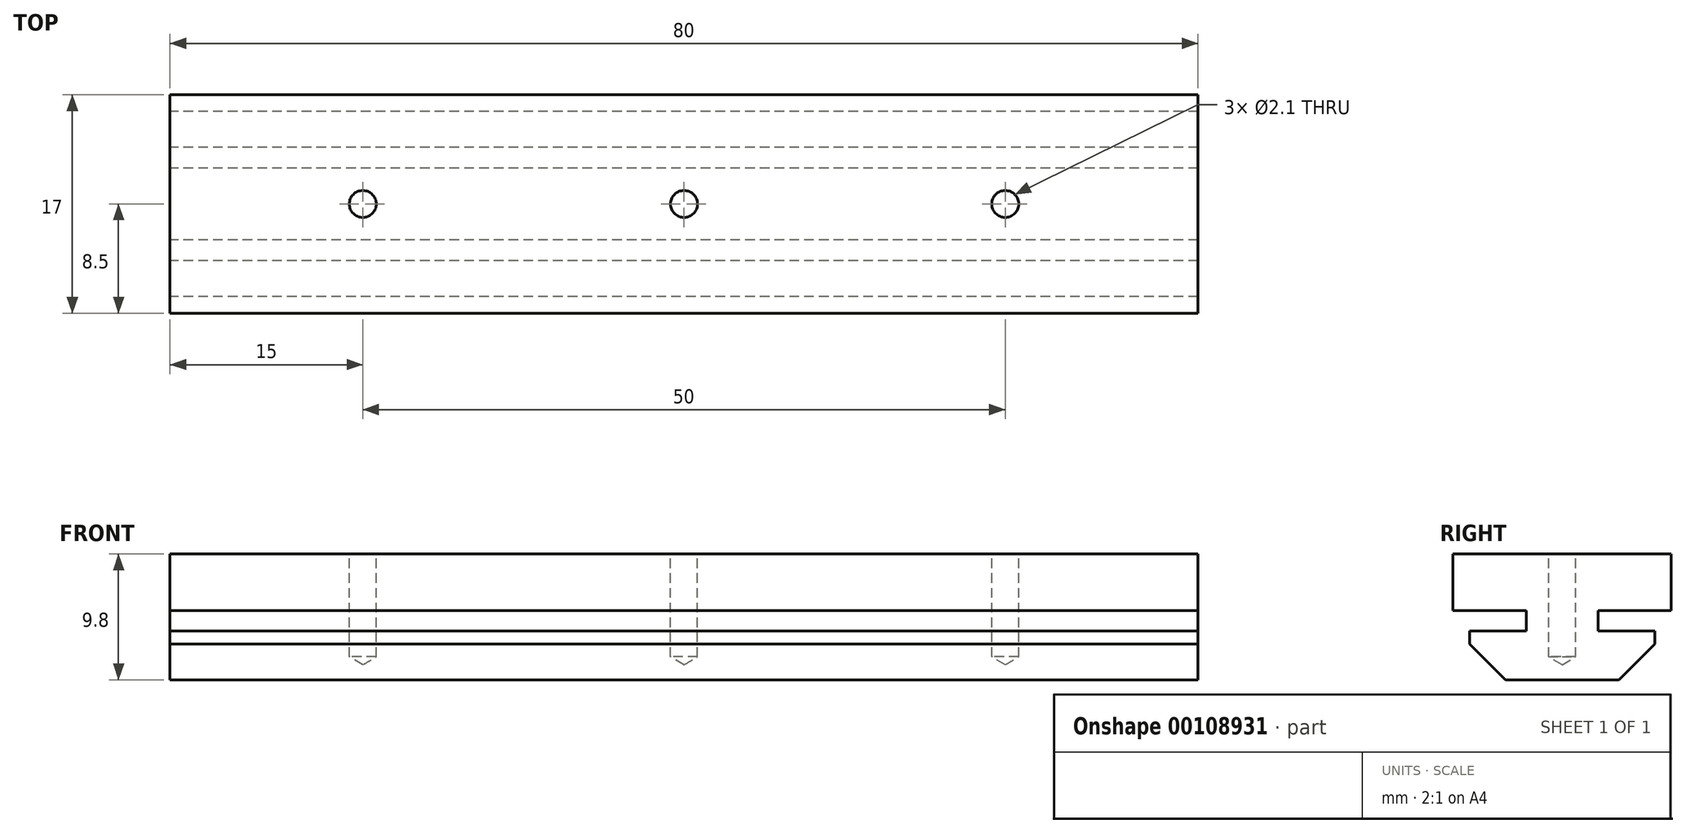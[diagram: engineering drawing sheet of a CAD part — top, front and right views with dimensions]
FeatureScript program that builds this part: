
annotation { "Feature Type Name" : "Feature", "Feature Type Description" : "" }
export const myFeature = defineFeature(function(context is Context, id is Id, definition is map)
    precondition{}
    {
        {
            var Q0;
            Q0=qCreatedBy(makeId("Top.planeOp"),FACE);
            var sketch = newSketch(context, id + "F0", { "sketchPlane" : qUnion([Q0])});
            skLineSegment(sketch, "E0.bottom", {"start": v(40, -8.5) * mm, "end": v(-40, -8.5) * mm});
            skLineSegment(sketch, "E0.top", {"start": v(40, 8.5) * mm, "end": v(-40, 8.5) * mm});
            skLineSegment(sketch, "E0.left", {"start": v(40, -8.5) * mm, "end": v(40, 8.5) * mm});
            skLineSegment(sketch, "E0.right", {"start": v(-40, -8.5) * mm, "end": v(-40, 8.5) * mm});
            skPoint(sketch, "E0.middle", {"position": v(0, 0) * mm});
            skSolve(sketch);
        }
        {
            var Q0;
            Q0=makeQuery(id+"F0.imprint","IMPRINT",FACE,{"disambiguationData":[TD([[makeQuery(id+"F0.imprint","IMPRINT",EDGE,{"derivedFrom":sQuery(id+"F0.wireOp",EDGE,"E0.bottom")}),-1.0]])]});
            extrude(context, id + "F1", {"entities" : qUnion([Q0]), "endBound" : BoundingType.SYMMETRIC, "depth" : 9.8 * mm});
        }
        {
            var Q0;
            Q0=makeQuery(id+"F1.opExtrude","SWEPT_FACE",FACE,{"disambiguationData":[OSD([sQuery(id+"F0.wireOp",EDGE,"E0.right")])]});
            var sketch = newSketch(context, id + "F2", { "sketchPlane" : qUnion([Q0])});
            skLineSegment(sketch, "E1", {"start": v(-8.5, 0.5) * mm, "end": v(-2.8, 0.5) * mm});
            skLineSegment(sketch, "E2", {"start": v(-2.8, 0.5) * mm, "end": v(-2.8, -1.1) * mm});
            skLineSegment(sketch, "E3", {"start": v(-2.8, -1.1) * mm, "end": v(-7.2, -1.1) * mm});
            skLineSegment(sketch, "E4", {"start": v(-7.2, -1.1) * mm, "end": v(-7.2, -2.11) * mm});
            skLineSegment(sketch, "E5", {"start": v(-7.2, -2.11) * mm, "end": v(-4.41, -4.9) * mm});
            skLineSegment(sketch, "E6", {"start": v(0, 4.9) * mm, "end": v(0, -4.9) * mm, "construction": true});
            skLineSegment(sketch, "E7.MirrorCS", {"start": v(2.8, 0.5) * mm, "end": v(2.8, -1.1) * mm});
            skLineSegment(sketch, "E8.MirrorCS", {"start": v(8.5, 0.5) * mm, "end": v(2.8, 0.5) * mm});
            skLineSegment(sketch, "E9.MirrorCS", {"start": v(2.8, -1.1) * mm, "end": v(7.2, -1.1) * mm});
            skLineSegment(sketch, "E10.MirrorCS", {"start": v(7.2, -1.1) * mm, "end": v(7.2, -2.11) * mm});
            skLineSegment(sketch, "E11.MirrorCS", {"start": v(7.2, -2.11) * mm, "end": v(4.41, -4.9) * mm});
            skLineSegment(sketch, "E12", {"start": v(-8.5, 0.5) * mm, "end": v(-8.5, -4.9) * mm});
            skLineSegment(sketch, "E13", {"start": v(-8.5, -4.9) * mm, "end": v(-4.41, -4.9) * mm});
            skLineSegment(sketch, "E14", {"start": v(4.41, -4.9) * mm, "end": v(8.5, -4.9) * mm});
            skLineSegment(sketch, "E15", {"start": v(8.5, -4.9) * mm, "end": v(8.5, 0.5) * mm});
            skSolve(sketch);
        }
        {
            var Q0;
            Q0 = qSketchRegion(id + "F2", true);
            extrude(context, id + "F3", {"entities" : qUnion([Q0]), "operationType" : NewBodyOperationType.REMOVE, "endBound" : BoundingType.THROUGH_ALL, "oppositeDirection" : true, "depth" : 25 * mm});
        }
        {
            var Q0;
            Q0=makeQuery(id+"F1.opExtrude","CAP_FACE",FACE,{"disambiguationData":[OSD([sQuery(id+"F0.wireOp",EDGE,"E0.bottom"),sQuery(id+"F0.wireOp",EDGE,"E0.top"),sQuery(id+"F0.wireOp",EDGE,"E0.left"),sQuery(id+"F0.wireOp",EDGE,"E0.right")])],"isStart":false});
            var sketch = newSketch(context, id + "F4", { "sketchPlane" : qUnion([Q0])});
            skPoint(sketch, "E16", {"position": v(0, 0) * mm});
            skPoint(sketch, "E17", {"position": v(25, 0) * mm});
            skPoint(sketch, "E18", {"position": v(-25, 0) * mm});
            skLineSegment(sketch, "E19", {"start": v(-25, 0) * mm, "end": v(0, 0) * mm, "construction": true});
            skLineSegment(sketch, "E20", {"start": v(25, 0) * mm, "end": v(0, 0) * mm, "construction": true});
            skSolve(sketch);
        }
        {
            var Q0;
            Q0=sQuery(id+"F4.wireOp",VERTEX,"E18");
            var Q1;
            Q1=sQuery(id+"F4.wireOp",VERTEX,"E17");
            var Q2;
            Q2=sQuery(id+"F4.wireOp",VERTEX,"E16");
            var Q3;
            Q3=makeQuery(id+"F1.opExtrude","SWEPT_BODY",BODY,{"disambiguationData":[OSD([sQuery(id+"F0.wireOp",EDGE,"E0.bottom"),sQuery(id+"F0.wireOp",EDGE,"E0.top"),sQuery(id+"F0.wireOp",EDGE,"E0.left"),sQuery(id+"F0.wireOp",EDGE,"E0.right")])]});
            hole(context, id + "F5", {"style" : HoleStyle.SIMPLE, "endStyle" : HoleEndStyle.BLIND, "standardTappedOrClearance" : lookupTablePath({ "standard" : "ISO", "size" : "2.1", "type" : "Drilled" }), "standardBlindInLast" : lookupTablePath({ "standard" : "ISO", "size" : "2.1", "type" : "Drilled" }), "holeDiameter" : 2.1 * mm, "holeDepth" : 8 * mm, "locations" : qUnion([Q0, Q1, Q2]), "scope" : qUnion([Q3])});
        }
    });
